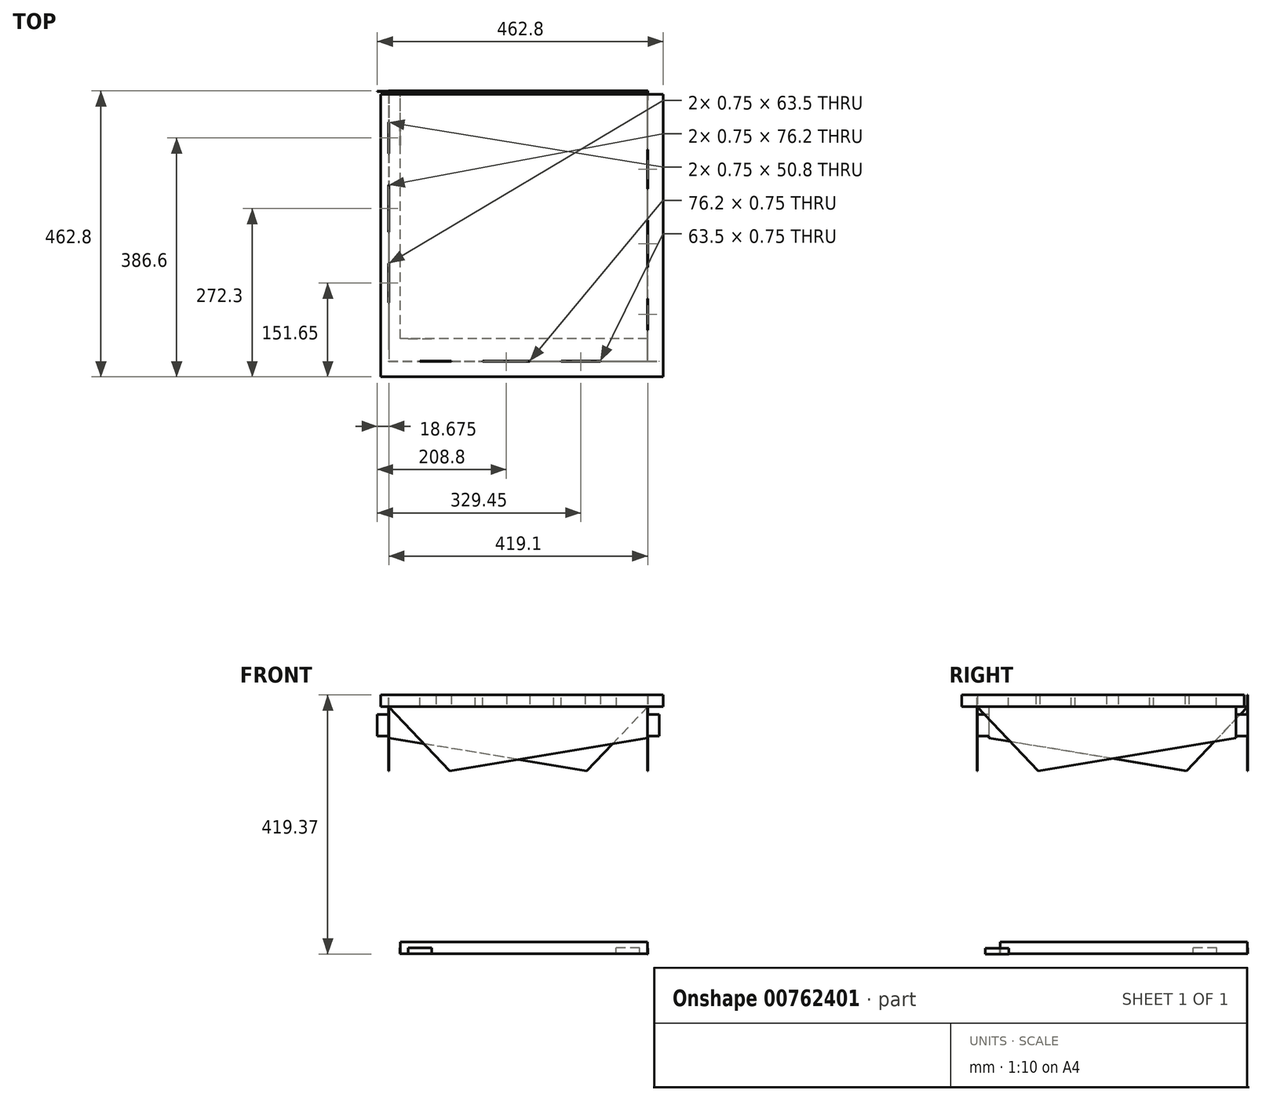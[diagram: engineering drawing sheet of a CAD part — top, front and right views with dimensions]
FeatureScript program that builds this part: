
annotation { "Feature Type Name" : "Feature", "Feature Type Description" : "" }
export const myFeature = defineFeature(function(context is Context, id is Id, definition is map)
    precondition{}
    {
        {
            assignVariable(context, id + "F0", {"name" : "PLY", "anyValue" : 0.75});
        }
        {
            var Q0;
            Q0=qCreatedBy(makeId("Front.planeOp"),FACE);
            var sketch = newSketch(context, id + "F1", { "sketchPlane" : qUnion([Q0])});
            skLineSegment(sketch, "E0", {"start": v(0, 0) * mm, "end": v(50.8, 0) * mm});
            skLineSegment(sketch, "E1", {"start": v(50.8, 0) * mm, "end": v(0, 0) * mm});
            skLineSegment(sketch, "E2", {"start": v(0, 0) * mm, "end": v(0, 762) * mm});
            skLineSegment(sketch, "E3", {"start": v(0, 762) * mm, "end": v(50.8, 762) * mm});
            skLineSegment(sketch, "E4", {"start": v(419.1, 762) * mm, "end": v(419.1, 711.2) * mm});
            skLineSegment(sketch, "E5", {"start": v(0, 762) * mm, "end": v(99.29, 658.14) * mm});
            skLineSegment(sketch, "E6", {"start": v(99.29, 658.14) * mm, "end": v(419.1, 711.2) * mm});
            skLineSegment(sketch, "E7", {"start": v(50.8, 0) * mm, "end": v(99.29, 658.14) * mm});
            skLineSegment(sketch, "E8", {"start": v(50.8, 762) * mm, "end": v(50.8, 781.05) * mm});
            skLineSegment(sketch, "E9", {"start": v(50.8, 781.05) * mm, "end": v(101.6, 781.05) * mm});
            skLineSegment(sketch, "E10", {"start": v(101.6, 781.05) * mm, "end": v(101.6, 762) * mm});
            skLineSegment(sketch, "E11", {"start": v(101.6, 762) * mm, "end": v(152.4, 762) * mm});
            skLineSegment(sketch, "E12", {"start": v(152.4, 762) * mm, "end": v(152.4, 781.05) * mm});
            skLineSegment(sketch, "E13", {"start": v(152.4, 781.05) * mm, "end": v(228.6, 781.05) * mm});
            skLineSegment(sketch, "E14", {"start": v(228.6, 781.05) * mm, "end": v(228.6, 762) * mm});
            skLineSegment(sketch, "E15", {"start": v(228.6, 762) * mm, "end": v(279.4, 762) * mm});
            skLineSegment(sketch, "E16", {"start": v(279.4, 762) * mm, "end": v(279.4, 781.05) * mm});
            skLineSegment(sketch, "E17", {"start": v(279.4, 781.05) * mm, "end": v(342.9, 781.05) * mm});
            skLineSegment(sketch, "E18", {"start": v(342.9, 781.05) * mm, "end": v(342.9, 762) * mm});
            skLineSegment(sketch, "E19.trimOffspring", {"start": v(342.9, 762) * mm, "end": v(419.1, 762) * mm});
            skLineSegment(sketch, "E20", {"start": v(419.1, 749.3) * mm, "end": v(438.15, 749.3) * mm});
            skLineSegment(sketch, "E21", {"start": v(438.15, 749.3) * mm, "end": v(438.15, 714.38) * mm});
            skLineSegment(sketch, "E22", {"start": v(438.15, 714.38) * mm, "end": v(419.1, 714.38) * mm});
            skSolve(sketch);
        }
        {
            var Q0;
            Q0=makeQuery(id+"F1.imprint","IMPRINT",FACE,{"disambiguationData":[TD([[makeQuery(id+"F1.imprint","IMPRINT",EDGE,{"derivedFrom":sQuery(id+"F1.wireOp",EDGE,"E1")}),-1.0]])]});
            var Q1;
            Q1=makeQuery(id+"F1.imprint","IMPRINT",FACE,{"disambiguationData":[TD([[makeQuery(id+"F1.imprint","IMPRINT",EDGE,{"derivedFrom":sQuery(id+"F1.wireOp",EDGE,"E3")}),-1.0]])]});
            var Q2;
            Q2=makeQuery(id+"F1.imprint","IMPRINT",FACE,{"disambiguationData":[TD([[makeQuery(id+"F1.imprint","IMPRINT",EDGE,{"derivedFrom":sQuery(id+"F1.wireOp",EDGE,"E4")}),-1.0]])]});
            extrude(context, id + "F2", {"entities" : qUnion([Q0, Q1, Q2]), "depth" : (getVariable(context, 'PLY')) * mm, "offsetDistance" : 25.4 * mm});
        }
        {
            var Q0;
            Q0=makeQuery(id+"F2.opExtrude","SWEPT_FACE",FACE,{"disambiguationData":[OSD([sQuery(id+"F1.wireOp",EDGE,"E3")])]});
            var sketch = newSketch(context, id + "F3", { "sketchPlane" : qUnion([Q0])});
            skLineSegment(sketch, "E23", {"start": v(-12.7, -25.4) * mm, "end": v(-12.7, 431.8) * mm});
            skLineSegment(sketch, "E24", {"start": v(-12.7, 431.8) * mm, "end": v(444.5, 431.8) * mm});
            skLineSegment(sketch, "E25", {"start": v(444.5, 431.8) * mm, "end": v(444.5, -25.4) * mm});
            skLineSegment(sketch, "E26", {"start": v(-12.7, -25.4) * mm, "end": v(444.5, -25.4) * mm});
            skLineSegment(sketch, "E27", {"start": v(444.5, -25.4) * mm, "end": v(-12.7, 431.8) * mm});
            skLineSegment(sketch, "E28", {"start": v(-12.7, -25.4) * mm, "end": v(444.5, 431.8) * mm});
            skPoint(sketch, "E29", {"position": v(215.9, 203.2) * mm});
            skSolve(sketch);
        }
        {
            var Q0;
            Q0 = qSketchRegion(id + "F3", true);
            extrude(context, id + "F4", {"entities" : qUnion([Q0]), "depth" : 19.05 * mm, "offsetDistance" : 25.4 * mm});
        }
        {
            var Q0;
            {var subQ0=sQuery(id+"F1.wireOp",EDGE,"E20");Q0=makeQuery(id+"F1.imprint","IMPRINT",FACE,{"disambiguationData":[TD([[makeQuery(id+"F1.imprint","IMPRINT",EDGE,{"derivedFrom":subQ0}),-1.0]])]});}
            extrude(context, id + "F5", {"entities" : qUnion([Q0]), "operationType" : NewBodyOperationType.ADD, "depth" : (getVariable(context, 'PLY') / 2) * mm, "offsetDistance" : 25.4 * mm});
        }
        {
            var Q0;
            Q0=makeQuery(id+"F2.opExtrude","SWEPT_BODY",BODY,{"disambiguationData":[OSD([sQuery(id+"F1.wireOp",EDGE,"E1"),sQuery(id+"F1.wireOp",EDGE,"E2"),sQuery(id+"F1.wireOp",EDGE,"E4"),sQuery(id+"F1.wireOp",EDGE,"E6"),sQuery(id+"F1.wireOp",EDGE,"E7"),sQuery(id+"F1.wireOp",EDGE,"E3"),sQuery(id+"F1.wireOp",EDGE,"E8"),sQuery(id+"F1.wireOp",EDGE,"E9"),sQuery(id+"F1.wireOp",EDGE,"E10"),sQuery(id+"F1.wireOp",EDGE,"E12"),sQuery(id+"F1.wireOp",EDGE,"E13"),sQuery(id+"F1.wireOp",EDGE,"E14"),sQuery(id+"F1.wireOp",EDGE,"E16"),sQuery(id+"F1.wireOp",EDGE,"E17"),sQuery(id+"F1.wireOp",EDGE,"E18"),sQuery(id+"F1.wireOp",EDGE,"E11"),sQuery(id+"F1.wireOp",EDGE,"E15"),sQuery(id+"F1.wireOp",EDGE,"E19.trimOffspring")])]});
            var Q1;
            Q1=makeQuery(id+"F2.opExtrude","CAP_EDGE",EDGE,{"disambiguationData":[OSD([sQuery(id+"F1.wireOp",EDGE,"E4")])],"isStart":false});
            transform(context, id + "F6", {"entities" : qUnion([Q0]), "transformType" : TransformType.ROTATION, "transformAxis" : qUnion([Q1]), "angle" : 90 * degree, "oppositeDirection" : true, "makeCopy" : true});
        }
        {
            var Q0;
            Q0=makeQuery(id+"F6.opPattern","COPY",BODY,{"derivedFrom":makeQuery(id+"F2.opExtrude","SWEPT_BODY",BODY,{"disambiguationData":[OSD([sQuery(id+"F1.wireOp",EDGE,"E1"),sQuery(id+"F1.wireOp",EDGE,"E2"),sQuery(id+"F1.wireOp",EDGE,"E4"),sQuery(id+"F1.wireOp",EDGE,"E6"),sQuery(id+"F1.wireOp",EDGE,"E7"),sQuery(id+"F1.wireOp",EDGE,"E3"),sQuery(id+"F1.wireOp",EDGE,"E8"),sQuery(id+"F1.wireOp",EDGE,"E9"),sQuery(id+"F1.wireOp",EDGE,"E10"),sQuery(id+"F1.wireOp",EDGE,"E12"),sQuery(id+"F1.wireOp",EDGE,"E13"),sQuery(id+"F1.wireOp",EDGE,"E14"),sQuery(id+"F1.wireOp",EDGE,"E16"),sQuery(id+"F1.wireOp",EDGE,"E17"),sQuery(id+"F1.wireOp",EDGE,"E18"),sQuery(id+"F1.wireOp",EDGE,"E11"),sQuery(id+"F1.wireOp",EDGE,"E15"),sQuery(id+"F1.wireOp",EDGE,"E19.trimOffspring")])]}),"instanceName":"1"});
            var Q1;
            Q1=makeQuery(id+"F6.opPattern","COPY",VERTEX,{"derivedFrom":makeQuery(id+"F2.opExtrude","CAP_VERTEX",VERTEX,{"disambiguationData":[OSD([sQuery(id+"F1.wireOp",EDGE,"E2"),sQuery(id+"F1.wireOp",EDGE,"E5"),sQuery(id+"F1.wireOp",EDGE,"E3")])],"isStart":true}),"instanceName":"1"});
            var Q2;
            Q2=makeQuery(id+"F2.opExtrude","CAP_VERTEX",VERTEX,{"disambiguationData":[OSD([sQuery(id+"F1.wireOp",EDGE,"E4"),sQuery(id+"F1.wireOp",EDGE,"E19.trimOffspring")])],"isStart":false});
            transform(context, id + "F7", {"entities" : qUnion([Q0]), "transformType" : TransformType.TRANSLATION_ENTITY, "oppositeDirectionEntity" : false, "transformLine" : qUnion([Q1, Q2]), "makeCopy" : false});
        }
        {
            var Q0;
            Q0=makeQuery(id+"F6.opPattern","COPY",BODY,{"derivedFrom":makeQuery(id+"F2.opExtrude","SWEPT_BODY",BODY,{"disambiguationData":[OSD([sQuery(id+"F1.wireOp",EDGE,"E1"),sQuery(id+"F1.wireOp",EDGE,"E2"),sQuery(id+"F1.wireOp",EDGE,"E4"),sQuery(id+"F1.wireOp",EDGE,"E6"),sQuery(id+"F1.wireOp",EDGE,"E7"),sQuery(id+"F1.wireOp",EDGE,"E3"),sQuery(id+"F1.wireOp",EDGE,"E8"),sQuery(id+"F1.wireOp",EDGE,"E9"),sQuery(id+"F1.wireOp",EDGE,"E10"),sQuery(id+"F1.wireOp",EDGE,"E12"),sQuery(id+"F1.wireOp",EDGE,"E13"),sQuery(id+"F1.wireOp",EDGE,"E14"),sQuery(id+"F1.wireOp",EDGE,"E16"),sQuery(id+"F1.wireOp",EDGE,"E17"),sQuery(id+"F1.wireOp",EDGE,"E18"),sQuery(id+"F1.wireOp",EDGE,"E11"),sQuery(id+"F1.wireOp",EDGE,"E15"),sQuery(id+"F1.wireOp",EDGE,"E19.trimOffspring")])]}),"instanceName":"1"});
            var Q1;
            Q1=makeQuery(id+"F2.opExtrude","SWEPT_BODY",BODY,{"disambiguationData":[OSD([sQuery(id+"F1.wireOp",EDGE,"E1"),sQuery(id+"F1.wireOp",EDGE,"E2"),sQuery(id+"F1.wireOp",EDGE,"E4"),sQuery(id+"F1.wireOp",EDGE,"E6"),sQuery(id+"F1.wireOp",EDGE,"E7"),sQuery(id+"F1.wireOp",EDGE,"E3"),sQuery(id+"F1.wireOp",EDGE,"E8"),sQuery(id+"F1.wireOp",EDGE,"E9"),sQuery(id+"F1.wireOp",EDGE,"E10"),sQuery(id+"F1.wireOp",EDGE,"E12"),sQuery(id+"F1.wireOp",EDGE,"E13"),sQuery(id+"F1.wireOp",EDGE,"E14"),sQuery(id+"F1.wireOp",EDGE,"E16"),sQuery(id+"F1.wireOp",EDGE,"E17"),sQuery(id+"F1.wireOp",EDGE,"E18"),sQuery(id+"F1.wireOp",EDGE,"E11"),sQuery(id+"F1.wireOp",EDGE,"E15"),sQuery(id+"F1.wireOp",EDGE,"E19.trimOffspring")])]});
            var Q2;
            Q2=makeQuery(id+"F6.opPattern","COPY",EDGE,{"derivedFrom":makeQuery(id+"F5.opExtrude","CAP_EDGE",EDGE,{"disambiguationData":[OSD([sQuery(id+"F1.wireOp",EDGE,"E21")])],"isStart":false}),"instanceName":"1"});
            transform(context, id + "F8", {"entities" : qUnion([Q0, Q1]), "transformType" : TransformType.ROTATION, "transformAxis" : qUnion([Q2]), "angle" : 180 * degree, "makeCopy" : true});
        }
        {
            var Q0;
            Q0=makeQuery(id+"F8.opPattern","COPY",BODY,{"derivedFrom":makeQuery(id+"F6.opPattern","COPY",BODY,{"derivedFrom":makeQuery(id+"F2.opExtrude","SWEPT_BODY",BODY,{"disambiguationData":[OSD([sQuery(id+"F1.wireOp",EDGE,"E1"),sQuery(id+"F1.wireOp",EDGE,"E2"),sQuery(id+"F1.wireOp",EDGE,"E4"),sQuery(id+"F1.wireOp",EDGE,"E6"),sQuery(id+"F1.wireOp",EDGE,"E7"),sQuery(id+"F1.wireOp",EDGE,"E3"),sQuery(id+"F1.wireOp",EDGE,"E8"),sQuery(id+"F1.wireOp",EDGE,"E9"),sQuery(id+"F1.wireOp",EDGE,"E10"),sQuery(id+"F1.wireOp",EDGE,"E12"),sQuery(id+"F1.wireOp",EDGE,"E13"),sQuery(id+"F1.wireOp",EDGE,"E14"),sQuery(id+"F1.wireOp",EDGE,"E16"),sQuery(id+"F1.wireOp",EDGE,"E17"),sQuery(id+"F1.wireOp",EDGE,"E18"),sQuery(id+"F1.wireOp",EDGE,"E11"),sQuery(id+"F1.wireOp",EDGE,"E15"),sQuery(id+"F1.wireOp",EDGE,"E19.trimOffspring")])]}),"instanceName":"1"}),"instanceName":"1"});
            var Q1;
            Q1=makeQuery(id+"F8.opPattern","COPY",BODY,{"derivedFrom":makeQuery(id+"F2.opExtrude","SWEPT_BODY",BODY,{"disambiguationData":[OSD([sQuery(id+"F1.wireOp",EDGE,"E1"),sQuery(id+"F1.wireOp",EDGE,"E2"),sQuery(id+"F1.wireOp",EDGE,"E4"),sQuery(id+"F1.wireOp",EDGE,"E6"),sQuery(id+"F1.wireOp",EDGE,"E7"),sQuery(id+"F1.wireOp",EDGE,"E3"),sQuery(id+"F1.wireOp",EDGE,"E8"),sQuery(id+"F1.wireOp",EDGE,"E9"),sQuery(id+"F1.wireOp",EDGE,"E10"),sQuery(id+"F1.wireOp",EDGE,"E12"),sQuery(id+"F1.wireOp",EDGE,"E13"),sQuery(id+"F1.wireOp",EDGE,"E14"),sQuery(id+"F1.wireOp",EDGE,"E16"),sQuery(id+"F1.wireOp",EDGE,"E17"),sQuery(id+"F1.wireOp",EDGE,"E18"),sQuery(id+"F1.wireOp",EDGE,"E11"),sQuery(id+"F1.wireOp",EDGE,"E15"),sQuery(id+"F1.wireOp",EDGE,"E19.trimOffspring")])]}),"instanceName":"1"});
            transform(context, id + "F9", {"entities" : qUnion([Q0, Q1]), "transformType" : TransformType.TRANSLATION_3D, "dx" : -419.1 * mm, "dy" : -438.15 * mm, "dz" : 0 * mm, "makeCopy" : false});
        }
        {
            var Q0;
            Q0=makeQuery(id+"F8.opPattern","COPY",BODY,{"derivedFrom":makeQuery(id+"F6.opPattern","COPY",BODY,{"derivedFrom":makeQuery(id+"F2.opExtrude","SWEPT_BODY",BODY,{"disambiguationData":[OSD([sQuery(id+"F1.wireOp",EDGE,"E1"),sQuery(id+"F1.wireOp",EDGE,"E2"),sQuery(id+"F1.wireOp",EDGE,"E4"),sQuery(id+"F1.wireOp",EDGE,"E6"),sQuery(id+"F1.wireOp",EDGE,"E7"),sQuery(id+"F1.wireOp",EDGE,"E3"),sQuery(id+"F1.wireOp",EDGE,"E8"),sQuery(id+"F1.wireOp",EDGE,"E9"),sQuery(id+"F1.wireOp",EDGE,"E10"),sQuery(id+"F1.wireOp",EDGE,"E12"),sQuery(id+"F1.wireOp",EDGE,"E13"),sQuery(id+"F1.wireOp",EDGE,"E14"),sQuery(id+"F1.wireOp",EDGE,"E16"),sQuery(id+"F1.wireOp",EDGE,"E17"),sQuery(id+"F1.wireOp",EDGE,"E18"),sQuery(id+"F1.wireOp",EDGE,"E11"),sQuery(id+"F1.wireOp",EDGE,"E15"),sQuery(id+"F1.wireOp",EDGE,"E19.trimOffspring")])]}),"instanceName":"1"}),"instanceName":"1"});
            var Q1;
            Q1=makeQuery(id+"F2.opExtrude","SWEPT_BODY",BODY,{"disambiguationData":[OSD([sQuery(id+"F1.wireOp",EDGE,"E1"),sQuery(id+"F1.wireOp",EDGE,"E2"),sQuery(id+"F1.wireOp",EDGE,"E4"),sQuery(id+"F1.wireOp",EDGE,"E6"),sQuery(id+"F1.wireOp",EDGE,"E7"),sQuery(id+"F1.wireOp",EDGE,"E3"),sQuery(id+"F1.wireOp",EDGE,"E8"),sQuery(id+"F1.wireOp",EDGE,"E9"),sQuery(id+"F1.wireOp",EDGE,"E10"),sQuery(id+"F1.wireOp",EDGE,"E12"),sQuery(id+"F1.wireOp",EDGE,"E13"),sQuery(id+"F1.wireOp",EDGE,"E14"),sQuery(id+"F1.wireOp",EDGE,"E16"),sQuery(id+"F1.wireOp",EDGE,"E17"),sQuery(id+"F1.wireOp",EDGE,"E18"),sQuery(id+"F1.wireOp",EDGE,"E11"),sQuery(id+"F1.wireOp",EDGE,"E15"),sQuery(id+"F1.wireOp",EDGE,"E19.trimOffspring")])]});
            booleanBodies(context, id + "F10", {"operationType" : BooleanOperationType.SUBTRACTION, "tools" : qUnion([Q0]), "targets" : qUnion([Q1]), "keepTools" : true});
        }
        {
            var Q0;
            Q0=makeQuery(id+"F2.opExtrude","SWEPT_BODY",BODY,{"disambiguationData":[OSD([sQuery(id+"F1.wireOp",EDGE,"E1"),sQuery(id+"F1.wireOp",EDGE,"E2"),sQuery(id+"F1.wireOp",EDGE,"E4"),sQuery(id+"F1.wireOp",EDGE,"E6"),sQuery(id+"F1.wireOp",EDGE,"E7"),sQuery(id+"F1.wireOp",EDGE,"E3"),sQuery(id+"F1.wireOp",EDGE,"E8"),sQuery(id+"F1.wireOp",EDGE,"E9"),sQuery(id+"F1.wireOp",EDGE,"E10"),sQuery(id+"F1.wireOp",EDGE,"E12"),sQuery(id+"F1.wireOp",EDGE,"E13"),sQuery(id+"F1.wireOp",EDGE,"E14"),sQuery(id+"F1.wireOp",EDGE,"E16"),sQuery(id+"F1.wireOp",EDGE,"E17"),sQuery(id+"F1.wireOp",EDGE,"E18"),sQuery(id+"F1.wireOp",EDGE,"E11"),sQuery(id+"F1.wireOp",EDGE,"E15"),sQuery(id+"F1.wireOp",EDGE,"E19.trimOffspring")])]});
            var Q1;
            Q1=makeQuery(id+"F6.opPattern","COPY",BODY,{"derivedFrom":makeQuery(id+"F2.opExtrude","SWEPT_BODY",BODY,{"disambiguationData":[OSD([sQuery(id+"F1.wireOp",EDGE,"E1"),sQuery(id+"F1.wireOp",EDGE,"E2"),sQuery(id+"F1.wireOp",EDGE,"E4"),sQuery(id+"F1.wireOp",EDGE,"E6"),sQuery(id+"F1.wireOp",EDGE,"E7"),sQuery(id+"F1.wireOp",EDGE,"E3"),sQuery(id+"F1.wireOp",EDGE,"E8"),sQuery(id+"F1.wireOp",EDGE,"E9"),sQuery(id+"F1.wireOp",EDGE,"E10"),sQuery(id+"F1.wireOp",EDGE,"E12"),sQuery(id+"F1.wireOp",EDGE,"E13"),sQuery(id+"F1.wireOp",EDGE,"E14"),sQuery(id+"F1.wireOp",EDGE,"E16"),sQuery(id+"F1.wireOp",EDGE,"E17"),sQuery(id+"F1.wireOp",EDGE,"E18"),sQuery(id+"F1.wireOp",EDGE,"E11"),sQuery(id+"F1.wireOp",EDGE,"E15"),sQuery(id+"F1.wireOp",EDGE,"E19.trimOffspring")])]}),"instanceName":"1"});
            booleanBodies(context, id + "F11", {"operationType" : BooleanOperationType.SUBTRACTION, "tools" : qUnion([Q0]), "targets" : qUnion([Q1]), "keepTools" : true});
        }
        {
            var Q0;
            Q0=makeQuery(id+"F6.opPattern","COPY",BODY,{"derivedFrom":makeQuery(id+"F2.opExtrude","SWEPT_BODY",BODY,{"disambiguationData":[OSD([sQuery(id+"F1.wireOp",EDGE,"E1"),sQuery(id+"F1.wireOp",EDGE,"E2"),sQuery(id+"F1.wireOp",EDGE,"E4"),sQuery(id+"F1.wireOp",EDGE,"E6"),sQuery(id+"F1.wireOp",EDGE,"E7"),sQuery(id+"F1.wireOp",EDGE,"E3"),sQuery(id+"F1.wireOp",EDGE,"E8"),sQuery(id+"F1.wireOp",EDGE,"E9"),sQuery(id+"F1.wireOp",EDGE,"E10"),sQuery(id+"F1.wireOp",EDGE,"E12"),sQuery(id+"F1.wireOp",EDGE,"E13"),sQuery(id+"F1.wireOp",EDGE,"E14"),sQuery(id+"F1.wireOp",EDGE,"E16"),sQuery(id+"F1.wireOp",EDGE,"E17"),sQuery(id+"F1.wireOp",EDGE,"E18"),sQuery(id+"F1.wireOp",EDGE,"E11"),sQuery(id+"F1.wireOp",EDGE,"E15"),sQuery(id+"F1.wireOp",EDGE,"E19.trimOffspring")])]}),"instanceName":"1"});
            var Q1;
            Q1=makeQuery(id+"F8.opPattern","COPY",BODY,{"derivedFrom":makeQuery(id+"F2.opExtrude","SWEPT_BODY",BODY,{"disambiguationData":[OSD([sQuery(id+"F1.wireOp",EDGE,"E1"),sQuery(id+"F1.wireOp",EDGE,"E2"),sQuery(id+"F1.wireOp",EDGE,"E4"),sQuery(id+"F1.wireOp",EDGE,"E6"),sQuery(id+"F1.wireOp",EDGE,"E7"),sQuery(id+"F1.wireOp",EDGE,"E3"),sQuery(id+"F1.wireOp",EDGE,"E8"),sQuery(id+"F1.wireOp",EDGE,"E9"),sQuery(id+"F1.wireOp",EDGE,"E10"),sQuery(id+"F1.wireOp",EDGE,"E12"),sQuery(id+"F1.wireOp",EDGE,"E13"),sQuery(id+"F1.wireOp",EDGE,"E14"),sQuery(id+"F1.wireOp",EDGE,"E16"),sQuery(id+"F1.wireOp",EDGE,"E17"),sQuery(id+"F1.wireOp",EDGE,"E18"),sQuery(id+"F1.wireOp",EDGE,"E11"),sQuery(id+"F1.wireOp",EDGE,"E15"),sQuery(id+"F1.wireOp",EDGE,"E19.trimOffspring")])]}),"instanceName":"1"});
            booleanBodies(context, id + "F12", {"operationType" : BooleanOperationType.SUBTRACTION, "tools" : qUnion([Q0]), "targets" : qUnion([Q1]), "keepTools" : true});
        }
        {
            var Q0;
            Q0=makeQuery(id+"F8.opPattern","COPY",BODY,{"derivedFrom":makeQuery(id+"F2.opExtrude","SWEPT_BODY",BODY,{"disambiguationData":[OSD([sQuery(id+"F1.wireOp",EDGE,"E1"),sQuery(id+"F1.wireOp",EDGE,"E2"),sQuery(id+"F1.wireOp",EDGE,"E4"),sQuery(id+"F1.wireOp",EDGE,"E6"),sQuery(id+"F1.wireOp",EDGE,"E7"),sQuery(id+"F1.wireOp",EDGE,"E3"),sQuery(id+"F1.wireOp",EDGE,"E8"),sQuery(id+"F1.wireOp",EDGE,"E9"),sQuery(id+"F1.wireOp",EDGE,"E10"),sQuery(id+"F1.wireOp",EDGE,"E12"),sQuery(id+"F1.wireOp",EDGE,"E13"),sQuery(id+"F1.wireOp",EDGE,"E14"),sQuery(id+"F1.wireOp",EDGE,"E16"),sQuery(id+"F1.wireOp",EDGE,"E17"),sQuery(id+"F1.wireOp",EDGE,"E18"),sQuery(id+"F1.wireOp",EDGE,"E11"),sQuery(id+"F1.wireOp",EDGE,"E15"),sQuery(id+"F1.wireOp",EDGE,"E19.trimOffspring")])]}),"instanceName":"1"});
            var Q1;
            Q1=makeQuery(id+"F8.opPattern","COPY",BODY,{"derivedFrom":makeQuery(id+"F6.opPattern","COPY",BODY,{"derivedFrom":makeQuery(id+"F2.opExtrude","SWEPT_BODY",BODY,{"disambiguationData":[OSD([sQuery(id+"F1.wireOp",EDGE,"E1"),sQuery(id+"F1.wireOp",EDGE,"E2"),sQuery(id+"F1.wireOp",EDGE,"E4"),sQuery(id+"F1.wireOp",EDGE,"E6"),sQuery(id+"F1.wireOp",EDGE,"E7"),sQuery(id+"F1.wireOp",EDGE,"E3"),sQuery(id+"F1.wireOp",EDGE,"E8"),sQuery(id+"F1.wireOp",EDGE,"E9"),sQuery(id+"F1.wireOp",EDGE,"E10"),sQuery(id+"F1.wireOp",EDGE,"E12"),sQuery(id+"F1.wireOp",EDGE,"E13"),sQuery(id+"F1.wireOp",EDGE,"E14"),sQuery(id+"F1.wireOp",EDGE,"E16"),sQuery(id+"F1.wireOp",EDGE,"E17"),sQuery(id+"F1.wireOp",EDGE,"E18"),sQuery(id+"F1.wireOp",EDGE,"E11"),sQuery(id+"F1.wireOp",EDGE,"E15"),sQuery(id+"F1.wireOp",EDGE,"E19.trimOffspring")])]}),"instanceName":"1"}),"instanceName":"1"});
            booleanBodies(context, id + "F13", {"operationType" : BooleanOperationType.SUBTRACTION, "tools" : qUnion([Q0]), "targets" : qUnion([Q1]), "keepTools" : true});
        }
        {
            var Q0;
            Q0=makeQuery(id+"F2.opExtrude","SWEPT_BODY",BODY,{"disambiguationData":[OSD([sQuery(id+"F1.wireOp",EDGE,"E1"),sQuery(id+"F1.wireOp",EDGE,"E2"),sQuery(id+"F1.wireOp",EDGE,"E4"),sQuery(id+"F1.wireOp",EDGE,"E6"),sQuery(id+"F1.wireOp",EDGE,"E7"),sQuery(id+"F1.wireOp",EDGE,"E3"),sQuery(id+"F1.wireOp",EDGE,"E8"),sQuery(id+"F1.wireOp",EDGE,"E9"),sQuery(id+"F1.wireOp",EDGE,"E10"),sQuery(id+"F1.wireOp",EDGE,"E12"),sQuery(id+"F1.wireOp",EDGE,"E13"),sQuery(id+"F1.wireOp",EDGE,"E14"),sQuery(id+"F1.wireOp",EDGE,"E16"),sQuery(id+"F1.wireOp",EDGE,"E17"),sQuery(id+"F1.wireOp",EDGE,"E18"),sQuery(id+"F1.wireOp",EDGE,"E11"),sQuery(id+"F1.wireOp",EDGE,"E15"),sQuery(id+"F1.wireOp",EDGE,"E19.trimOffspring")])]});
            var Q1;
            Q1=makeQuery(id+"F8.opPattern","COPY",BODY,{"derivedFrom":makeQuery(id+"F6.opPattern","COPY",BODY,{"derivedFrom":makeQuery(id+"F2.opExtrude","SWEPT_BODY",BODY,{"disambiguationData":[OSD([sQuery(id+"F1.wireOp",EDGE,"E1"),sQuery(id+"F1.wireOp",EDGE,"E2"),sQuery(id+"F1.wireOp",EDGE,"E4"),sQuery(id+"F1.wireOp",EDGE,"E6"),sQuery(id+"F1.wireOp",EDGE,"E7"),sQuery(id+"F1.wireOp",EDGE,"E3"),sQuery(id+"F1.wireOp",EDGE,"E8"),sQuery(id+"F1.wireOp",EDGE,"E9"),sQuery(id+"F1.wireOp",EDGE,"E10"),sQuery(id+"F1.wireOp",EDGE,"E12"),sQuery(id+"F1.wireOp",EDGE,"E13"),sQuery(id+"F1.wireOp",EDGE,"E14"),sQuery(id+"F1.wireOp",EDGE,"E16"),sQuery(id+"F1.wireOp",EDGE,"E17"),sQuery(id+"F1.wireOp",EDGE,"E18"),sQuery(id+"F1.wireOp",EDGE,"E11"),sQuery(id+"F1.wireOp",EDGE,"E15"),sQuery(id+"F1.wireOp",EDGE,"E19.trimOffspring")])]}),"instanceName":"1"}),"instanceName":"1"});
            var Q2;
            Q2=makeQuery(id+"F8.opPattern","COPY",BODY,{"derivedFrom":makeQuery(id+"F2.opExtrude","SWEPT_BODY",BODY,{"disambiguationData":[OSD([sQuery(id+"F1.wireOp",EDGE,"E1"),sQuery(id+"F1.wireOp",EDGE,"E2"),sQuery(id+"F1.wireOp",EDGE,"E4"),sQuery(id+"F1.wireOp",EDGE,"E6"),sQuery(id+"F1.wireOp",EDGE,"E7"),sQuery(id+"F1.wireOp",EDGE,"E3"),sQuery(id+"F1.wireOp",EDGE,"E8"),sQuery(id+"F1.wireOp",EDGE,"E9"),sQuery(id+"F1.wireOp",EDGE,"E10"),sQuery(id+"F1.wireOp",EDGE,"E12"),sQuery(id+"F1.wireOp",EDGE,"E13"),sQuery(id+"F1.wireOp",EDGE,"E14"),sQuery(id+"F1.wireOp",EDGE,"E16"),sQuery(id+"F1.wireOp",EDGE,"E17"),sQuery(id+"F1.wireOp",EDGE,"E18"),sQuery(id+"F1.wireOp",EDGE,"E11"),sQuery(id+"F1.wireOp",EDGE,"E15"),sQuery(id+"F1.wireOp",EDGE,"E19.trimOffspring")])]}),"instanceName":"1"});
            var Q3;
            Q3=makeQuery(id+"F6.opPattern","COPY",BODY,{"derivedFrom":makeQuery(id+"F2.opExtrude","SWEPT_BODY",BODY,{"disambiguationData":[OSD([sQuery(id+"F1.wireOp",EDGE,"E1"),sQuery(id+"F1.wireOp",EDGE,"E2"),sQuery(id+"F1.wireOp",EDGE,"E4"),sQuery(id+"F1.wireOp",EDGE,"E6"),sQuery(id+"F1.wireOp",EDGE,"E7"),sQuery(id+"F1.wireOp",EDGE,"E3"),sQuery(id+"F1.wireOp",EDGE,"E8"),sQuery(id+"F1.wireOp",EDGE,"E9"),sQuery(id+"F1.wireOp",EDGE,"E10"),sQuery(id+"F1.wireOp",EDGE,"E12"),sQuery(id+"F1.wireOp",EDGE,"E13"),sQuery(id+"F1.wireOp",EDGE,"E14"),sQuery(id+"F1.wireOp",EDGE,"E16"),sQuery(id+"F1.wireOp",EDGE,"E17"),sQuery(id+"F1.wireOp",EDGE,"E18"),sQuery(id+"F1.wireOp",EDGE,"E11"),sQuery(id+"F1.wireOp",EDGE,"E15"),sQuery(id+"F1.wireOp",EDGE,"E19.trimOffspring")])]}),"instanceName":"1"});
            var Q4;
            Q4=makeQuery(id+"F4.opExtrude","SWEPT_BODY",BODY,{"disambiguationData":[OSD([sQuery(id+"F3.wireOp",EDGE,"E23"),sQuery(id+"F3.wireOp",EDGE,"E24"),sQuery(id+"F3.wireOp",EDGE,"E25"),sQuery(id+"F3.wireOp",EDGE,"E26")])]});
            booleanBodies(context, id + "F14", {"operationType" : BooleanOperationType.SUBTRACTION, "tools" : qUnion([Q0, Q1, Q2, Q3]), "targets" : qUnion([Q4]), "keepTools" : true});
        }
        {
            var Q0;
            {var subQ0=sQuery(id+"F1.wireOp",EDGE,"E4");Q0=makeQuery(id+"F8.opPattern","COPY",FACE,{"derivedFrom":makeQuery(id+"F5.boolean.opBoolean","MERGE",FACE,{"derivedFrom":[makeQuery(id+"F2.opExtrude","CAP_FACE",FACE,{"disambiguationData":[OSD([sQuery(id+"F1.wireOp",EDGE,"E1"),sQuery(id+"F1.wireOp",EDGE,"E2"),subQ0,sQuery(id+"F1.wireOp",EDGE,"E6"),sQuery(id+"F1.wireOp",EDGE,"E7"),sQuery(id+"F1.wireOp",EDGE,"E3"),sQuery(id+"F1.wireOp",EDGE,"E8"),sQuery(id+"F1.wireOp",EDGE,"E9"),sQuery(id+"F1.wireOp",EDGE,"E10"),sQuery(id+"F1.wireOp",EDGE,"E12"),sQuery(id+"F1.wireOp",EDGE,"E13"),sQuery(id+"F1.wireOp",EDGE,"E14"),sQuery(id+"F1.wireOp",EDGE,"E16"),sQuery(id+"F1.wireOp",EDGE,"E17"),sQuery(id+"F1.wireOp",EDGE,"E18"),sQuery(id+"F1.wireOp",EDGE,"E11"),sQuery(id+"F1.wireOp",EDGE,"E15"),sQuery(id+"F1.wireOp",EDGE,"E19.trimOffspring")])],"isStart":true}),makeQuery(id+"F5.opExtrude","CAP_FACE",FACE,{"disambiguationData":[OSD([subQ0,sQuery(id+"F1.wireOp",EDGE,"E20"),sQuery(id+"F1.wireOp",EDGE,"E21"),sQuery(id+"F1.wireOp",EDGE,"E22")])],"isStart":true})]}),"instanceName":"1"});}
            var sketch = newSketch(context, id + "F15", { "sketchPlane" : qUnion([Q0])});
            skLineSegment(sketch, "E30", {"start": v(438.15, 0) * mm, "end": v(438.15, 381) * mm});
            skLineSegment(sketch, "E31.bottom", {"start": v(438.15, 381) * mm, "end": v(419.1, 381) * mm});
            skLineSegment(sketch, "E31.top", {"start": v(438.15, 361.95) * mm, "end": v(419.1, 361.95) * mm});
            skLineSegment(sketch, "E31.left", {"start": v(438.15, 381) * mm, "end": v(438.15, 361.95) * mm});
            skLineSegment(sketch, "E31.right", {"start": v(419.1, 381) * mm, "end": v(419.1, 361.95) * mm});
            skLineSegment(sketch, "E32.bottom", {"start": v(419.1, 381) * mm, "end": v(19.05, 381) * mm});
            skLineSegment(sketch, "E32.top", {"start": v(419.1, 361.95) * mm, "end": v(19.05, 361.95) * mm});
            skLineSegment(sketch, "E32.right", {"start": v(19.05, 381) * mm, "end": v(19.05, 361.95) * mm});
            skSolve(sketch);
        }
        {
            var Q0;
            {var subQ0=sQuery(id+"F15.wireOp",EDGE,"E32.right");Q0=makeQuery(id+"F15.imprint","IMPRINT",FACE,{"disambiguationData":[TD([[makeQuery(id+"F15.imprint","IMPRINT",EDGE,{"derivedFrom":subQ0}),1.0]])]});}
            var Q1;
            {var subQ0=sQuery(id+"F15.wireOp",EDGE,"E31.right");Q1=makeQuery(id+"F15.imprint","IMPRINT",FACE,{"disambiguationData":[TD([[makeQuery(id+"F15.imprint","IMPRINT",EDGE,{"derivedFrom":subQ0}),-1.0]])]});}
            extrude(context, id + "F16", {"entities" : qUnion([Q0, Q1]), "depth" : 400.05 * mm, "offsetDistance" : 25.4 * mm});
        }
        {
            var Q0;
            Q0=makeQuery(id+"F16.opExtrude","CAP_FACE",FACE,{"disambiguationData":[OSD([sQuery(id+"F15.wireOp",EDGE,"E32.bottom"),sQuery(id+"F15.wireOp",EDGE,"E32.top"),sQuery(id+"F15.wireOp",EDGE,"E31.right"),sQuery(id+"F15.wireOp",EDGE,"E32.right")])],"isStart":false});
            var sketch = newSketch(context, id + "F17", { "sketchPlane" : qUnion([Q0])});
            skLineSegment(sketch, "E33", {"start": v(19.05, 361.95) * mm, "end": v(31.75, 361.95) * mm});
            skLineSegment(sketch, "E34.bottom", {"start": v(31.75, 361.95) * mm, "end": v(69.85, 361.95) * mm});
            skLineSegment(sketch, "E34.top", {"start": v(31.75, 371.48) * mm, "end": v(69.85, 371.48) * mm});
            skLineSegment(sketch, "E34.left", {"start": v(31.75, 361.95) * mm, "end": v(31.75, 371.48) * mm});
            skLineSegment(sketch, "E34.right", {"start": v(69.85, 361.95) * mm, "end": v(69.85, 371.48) * mm});
            skSolve(sketch);
        }
        {
            var Q0;
            Q0 = qSketchRegion(id + "F17", true);
            extrude(context, id + "F18", {"entities" : qUnion([Q0]), "operationType" : NewBodyOperationType.ADD, "depth" : (getVariable(context, 'PLY')) * mm, "offsetDistance" : 25.4 * mm});
        }
        {
            var Q0;
            Q0=makeQuery(id+"F16.opExtrude","SWEPT_FACE",FACE,{"disambiguationData":[OSD([sQuery(id+"F15.wireOp",EDGE,"E31.right")])]});
            var sketch = newSketch(context, id + "F19", { "sketchPlane" : qUnion([Q0])});
            skLineSegment(sketch, "E35", {"start": v(0, 361.95) * mm, "end": v(12.7, 361.95) * mm});
            skLineSegment(sketch, "E36.bottom", {"start": v(12.52, 361.68) * mm, "end": v(50.62, 361.68) * mm});
            skLineSegment(sketch, "E36.top", {"start": v(12.52, 371.2) * mm, "end": v(50.62, 371.2) * mm});
            skLineSegment(sketch, "E36.left", {"start": v(12.52, 361.68) * mm, "end": v(12.52, 371.2) * mm});
            skLineSegment(sketch, "E36.right", {"start": v(50.62, 361.68) * mm, "end": v(50.62, 371.2) * mm});
            skSolve(sketch);
        }
        {
            var Q0;
            Q0 = qSketchRegion(id + "F19", true);
            extrude(context, id + "F20", {"entities" : qUnion([Q0]), "operationType" : NewBodyOperationType.ADD, "depth" : (getVariable(context, 'PLY')) * mm, "offsetDistance" : 25.4 * mm});
        }
        {
            var Q0;
            Q0=makeQuery(id+"F16.opExtrude","CAP_FACE",FACE,{"disambiguationData":[OSD([sQuery(id+"F15.wireOp",EDGE,"E32.bottom"),sQuery(id+"F15.wireOp",EDGE,"E32.top"),sQuery(id+"F15.wireOp",EDGE,"E31.right"),sQuery(id+"F15.wireOp",EDGE,"E32.right")])],"isStart":true});
            var sketch = newSketch(context, id + "F21", { "sketchPlane" : qUnion([Q0])});
            skLineSegment(sketch, "E37", {"start": v(-419.1, 361.95) * mm, "end": v(-406.4, 361.95) * mm});
            skLineSegment(sketch, "E38.bottom", {"start": v(-406.4, 361.95) * mm, "end": v(-368.3, 361.95) * mm});
            skLineSegment(sketch, "E38.top", {"start": v(-406.4, 371.48) * mm, "end": v(-368.3, 371.48) * mm});
            skLineSegment(sketch, "E38.left", {"start": v(-406.4, 361.95) * mm, "end": v(-406.4, 371.48) * mm});
            skLineSegment(sketch, "E38.right", {"start": v(-368.3, 361.95) * mm, "end": v(-368.3, 371.48) * mm});
            skSolve(sketch);
        }
        {
            var Q0;
            Q0 = qSketchRegion(id + "F21", true);
            extrude(context, id + "F22", {"entities" : qUnion([Q0]), "operationType" : NewBodyOperationType.ADD, "depth" : (getVariable(context, 'PLY')) * mm, "offsetDistance" : 25.4 * mm});
        }
        {
            var Q0;
            Q0=makeQuery(id+"F16.opExtrude","SWEPT_FACE",FACE,{"disambiguationData":[OSD([sQuery(id+"F15.wireOp",EDGE,"E32.right")])]});
            var sketch = newSketch(context, id + "F23", { "sketchPlane" : qUnion([Q0])});
            skLineSegment(sketch, "E39", {"start": v(-400.05, 361.95) * mm, "end": v(-387.35, 361.95) * mm});
            skLineSegment(sketch, "E40.bottom", {"start": v(-387.35, 361.95) * mm, "end": v(-349.25, 361.95) * mm});
            skLineSegment(sketch, "E40.top", {"start": v(-387.35, 371.48) * mm, "end": v(-349.25, 371.48) * mm});
            skLineSegment(sketch, "E40.left", {"start": v(-387.35, 361.95) * mm, "end": v(-387.35, 371.48) * mm});
            skLineSegment(sketch, "E40.right", {"start": v(-349.25, 361.95) * mm, "end": v(-349.25, 371.48) * mm});
            skSolve(sketch);
        }
        {
            var Q0;
            Q0 = qSketchRegion(id + "F23", true);
            extrude(context, id + "F24", {"entities" : qUnion([Q0]), "operationType" : NewBodyOperationType.ADD, "depth" : (getVariable(context, 'PLY')) * mm, "offsetDistance" : 25.4 * mm});
        }
        {
            var Q0;
            Q0=makeQuery(id+"F16.opExtrude","SWEPT_BODY",BODY,{"disambiguationData":[OSD([sQuery(id+"F15.wireOp",EDGE,"E32.bottom"),sQuery(id+"F15.wireOp",EDGE,"E32.top"),sQuery(id+"F15.wireOp",EDGE,"E31.right"),sQuery(id+"F15.wireOp",EDGE,"E32.right")])]});
            var Q1;
            Q1=makeQuery(id+"F2.opExtrude","SWEPT_BODY",BODY,{"disambiguationData":[OSD([sQuery(id+"F1.wireOp",EDGE,"E1"),sQuery(id+"F1.wireOp",EDGE,"E2"),sQuery(id+"F1.wireOp",EDGE,"E4"),sQuery(id+"F1.wireOp",EDGE,"E6"),sQuery(id+"F1.wireOp",EDGE,"E7"),sQuery(id+"F1.wireOp",EDGE,"E3"),sQuery(id+"F1.wireOp",EDGE,"E8"),sQuery(id+"F1.wireOp",EDGE,"E9"),sQuery(id+"F1.wireOp",EDGE,"E10"),sQuery(id+"F1.wireOp",EDGE,"E12"),sQuery(id+"F1.wireOp",EDGE,"E13"),sQuery(id+"F1.wireOp",EDGE,"E14"),sQuery(id+"F1.wireOp",EDGE,"E16"),sQuery(id+"F1.wireOp",EDGE,"E17"),sQuery(id+"F1.wireOp",EDGE,"E18"),sQuery(id+"F1.wireOp",EDGE,"E11"),sQuery(id+"F1.wireOp",EDGE,"E15"),sQuery(id+"F1.wireOp",EDGE,"E19.trimOffspring")])]});
            var Q2;
            Q2=makeQuery(id+"F6.opPattern","COPY",BODY,{"derivedFrom":makeQuery(id+"F2.opExtrude","SWEPT_BODY",BODY,{"disambiguationData":[OSD([sQuery(id+"F1.wireOp",EDGE,"E1"),sQuery(id+"F1.wireOp",EDGE,"E2"),sQuery(id+"F1.wireOp",EDGE,"E4"),sQuery(id+"F1.wireOp",EDGE,"E6"),sQuery(id+"F1.wireOp",EDGE,"E7"),sQuery(id+"F1.wireOp",EDGE,"E3"),sQuery(id+"F1.wireOp",EDGE,"E8"),sQuery(id+"F1.wireOp",EDGE,"E9"),sQuery(id+"F1.wireOp",EDGE,"E10"),sQuery(id+"F1.wireOp",EDGE,"E12"),sQuery(id+"F1.wireOp",EDGE,"E13"),sQuery(id+"F1.wireOp",EDGE,"E14"),sQuery(id+"F1.wireOp",EDGE,"E16"),sQuery(id+"F1.wireOp",EDGE,"E17"),sQuery(id+"F1.wireOp",EDGE,"E18"),sQuery(id+"F1.wireOp",EDGE,"E11"),sQuery(id+"F1.wireOp",EDGE,"E15"),sQuery(id+"F1.wireOp",EDGE,"E19.trimOffspring")])]}),"instanceName":"1"});
            var Q3;
            Q3=makeQuery(id+"F8.opPattern","COPY",BODY,{"derivedFrom":makeQuery(id+"F2.opExtrude","SWEPT_BODY",BODY,{"disambiguationData":[OSD([sQuery(id+"F1.wireOp",EDGE,"E1"),sQuery(id+"F1.wireOp",EDGE,"E2"),sQuery(id+"F1.wireOp",EDGE,"E4"),sQuery(id+"F1.wireOp",EDGE,"E6"),sQuery(id+"F1.wireOp",EDGE,"E7"),sQuery(id+"F1.wireOp",EDGE,"E3"),sQuery(id+"F1.wireOp",EDGE,"E8"),sQuery(id+"F1.wireOp",EDGE,"E9"),sQuery(id+"F1.wireOp",EDGE,"E10"),sQuery(id+"F1.wireOp",EDGE,"E12"),sQuery(id+"F1.wireOp",EDGE,"E13"),sQuery(id+"F1.wireOp",EDGE,"E14"),sQuery(id+"F1.wireOp",EDGE,"E16"),sQuery(id+"F1.wireOp",EDGE,"E17"),sQuery(id+"F1.wireOp",EDGE,"E18"),sQuery(id+"F1.wireOp",EDGE,"E11"),sQuery(id+"F1.wireOp",EDGE,"E15"),sQuery(id+"F1.wireOp",EDGE,"E19.trimOffspring")])]}),"instanceName":"1"});
            var Q4;
            Q4=makeQuery(id+"F8.opPattern","COPY",BODY,{"derivedFrom":makeQuery(id+"F6.opPattern","COPY",BODY,{"derivedFrom":makeQuery(id+"F2.opExtrude","SWEPT_BODY",BODY,{"disambiguationData":[OSD([sQuery(id+"F1.wireOp",EDGE,"E1"),sQuery(id+"F1.wireOp",EDGE,"E2"),sQuery(id+"F1.wireOp",EDGE,"E4"),sQuery(id+"F1.wireOp",EDGE,"E6"),sQuery(id+"F1.wireOp",EDGE,"E7"),sQuery(id+"F1.wireOp",EDGE,"E3"),sQuery(id+"F1.wireOp",EDGE,"E8"),sQuery(id+"F1.wireOp",EDGE,"E9"),sQuery(id+"F1.wireOp",EDGE,"E10"),sQuery(id+"F1.wireOp",EDGE,"E12"),sQuery(id+"F1.wireOp",EDGE,"E13"),sQuery(id+"F1.wireOp",EDGE,"E14"),sQuery(id+"F1.wireOp",EDGE,"E16"),sQuery(id+"F1.wireOp",EDGE,"E17"),sQuery(id+"F1.wireOp",EDGE,"E18"),sQuery(id+"F1.wireOp",EDGE,"E11"),sQuery(id+"F1.wireOp",EDGE,"E15"),sQuery(id+"F1.wireOp",EDGE,"E19.trimOffspring")])]}),"instanceName":"1"}),"instanceName":"1"});
            booleanBodies(context, id + "F25", {"operationType" : BooleanOperationType.SUBTRACTION, "tools" : qUnion([Q0]), "targets" : qUnion([Q1, Q2, Q3, Q4]), "keepTools" : true});
        }
    });
